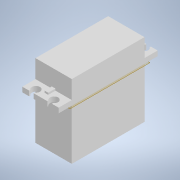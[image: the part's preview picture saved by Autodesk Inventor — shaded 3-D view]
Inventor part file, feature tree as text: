
AUTODESK INVENTOR PART (.ipt)
format: ipt  version: 2020 (Build 240168000, 168)  size: 172,032 bytes
history: native  units: in
note: dims shown in document units (in); Inventor stores cm internally (conversion verified against a paired STEP export)
features: extrude x4, sketch x4, projected_geometry x2, plane x1
ambient origin geometry x8: Origin, YZ Plane, XZ Plane, XY Plane, X Axis, Y Axis, Z Axis, Center Point
bodies: Solid1 (feature_tree)
feature tree (11):
  extrude  "Extrusion1"  Depth=1.5748in
  plane  "Work Plane1"
  extrude  "Extrusion2"  TaperAngle=0.0deg  [1 undecoded]
  extrude  "Extrusion3"  Depth=2.1457in
  extrude  "Extrusion4"  Depth=0.0394in
  sketch  "Sketch1"  dims[d0=0.7874in d1=1.5748in]
  sketch  "Sketch2"  dims[d2=1.0906in d3=0.0in d4=0.0in]
  projected_geometry  "Projected Loop1"
  sketch  "Sketch3"  dims[d5=0.5in d6=0.0in d7=2.1457in]
  projected_geometry  "Projected Loop2"
  sketch  "Sketch4"  dims[d8=0.3937in d9=1.9488in d10=0.1772in d11=0.1063in d12=0.0in d13=0.0984in d14=0.0787in d15=0.1575in d16=0.0394in d17=0.0in]
note: 1 required parameter value undecoded (feature->parameter linkage not recoverable at this tier; creation-order binding heuristic only, values carry confidence <= 0.55)
